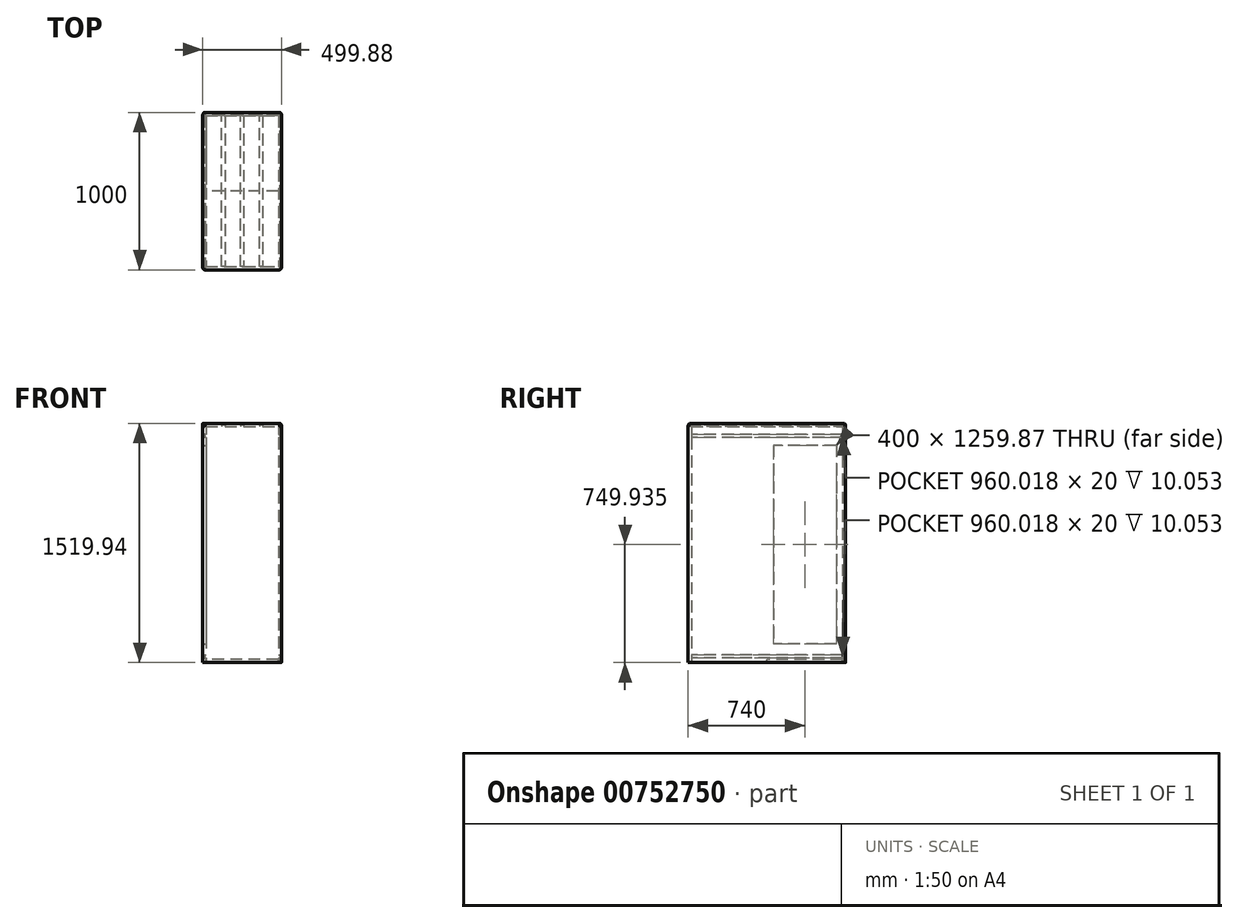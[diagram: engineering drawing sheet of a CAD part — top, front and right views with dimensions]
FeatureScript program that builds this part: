
annotation { "Feature Type Name" : "Feature", "Feature Type Description" : "" }
export const myFeature = defineFeature(function(context is Context, id is Id, definition is map)
    precondition{}
    {
        {
            var Q0;
            Q0=qCreatedBy(makeId("Top.planeOp"),FACE);
            var sketch = newSketch(context, id + "F0", { "sketchPlane" : qUnion([Q0])});
            skLineSegment(sketch, "E0.bottom", {"start": v(-249.94, -500) * mm, "end": v(249.94, -500) * mm});
            skLineSegment(sketch, "E0.top", {"start": v(-249.94, 500) * mm, "end": v(249.94, 500) * mm});
            skLineSegment(sketch, "E0.left", {"start": v(-249.94, -500) * mm, "end": v(-249.94, 500) * mm});
            skLineSegment(sketch, "E0.right", {"start": v(249.94, -500) * mm, "end": v(249.94, 500) * mm});
            skPoint(sketch, "E0.middle", {"position": v(0, 0) * mm});
            skLineSegment(sketch, "E1.0", {"start": v(-229.95, -480) * mm, "end": v(-229.95, 480) * mm});
            skLineSegment(sketch, "E1.1", {"start": v(-229.95, -480) * mm, "end": v(229.95, -480) * mm});
            skLineSegment(sketch, "E1.2", {"start": v(229.95, -480) * mm, "end": v(229.95, 480) * mm});
            skLineSegment(sketch, "E1.3", {"start": v(-229.95, 480) * mm, "end": v(229.95, 480) * mm});
            skLineSegment(sketch, "E2.top", {"start": v(-229.95, 0) * mm, "end": v(229.95, 0) * mm});
            skLineSegment(sketch, "E2.left", {"start": v(-229.95, -480) * mm, "end": v(-229.95, 0) * mm});
            skLineSegment(sketch, "E2.right", {"start": v(229.95, -480) * mm, "end": v(229.95, 0) * mm});
            skSolve(sketch);
        }
        {
            var Q0;
            Q0=makeQuery(id+"F0.imprint","IMPRINT",FACE,{"disambiguationData":[TD([[makeQuery(id+"F0.imprint","IMPRINT",EDGE,{"derivedFrom":sQuery(id+"F0.wireOp",EDGE,"E0.bottom")}),1.0]])]});
            extrude(context, id + "F1", {"entities" : qUnion([Q0]), "depth" : 5.9 * 254 * mm, "offsetDistance" : 25.4 * mm});
        }
        {
            var Q0;
            Q0=makeQuery(id+"F1.opExtrude","SWEPT_FACE",FACE,{"disambiguationData":[OSD([sQuery(id+"F0.wireOp",EDGE,"E0.right")])]});
            var sketch = newSketch(context, id + "F2", { "sketchPlane" : qUnion([Q0])});
            skLineSegment(sketch, "E3.bottom", {"start": v(-500, 1499.87) * mm, "end": v(500, 1499.87) * mm});
            skLineSegment(sketch, "E3.top", {"start": v(-500, 1519.94) * mm, "end": v(500, 1519.94) * mm});
            skLineSegment(sketch, "E3.left", {"start": v(-500, 1499.87) * mm, "end": v(-500, 1519.94) * mm});
            skLineSegment(sketch, "E3.right", {"start": v(500, 1499.87) * mm, "end": v(500, 1519.94) * mm});
            skSolve(sketch);
        }
        {
            var Q0;
            Q0=makeQuery(id+"F2.imprint","IMPRINT",FACE,{"disambiguationData":[TD([[makeQuery(id+"F2.imprint","IMPRINT",EDGE,{"derivedFrom":sQuery(id+"F2.wireOp",EDGE,"E3.bottom")}),1.0]])]});
            var Q1;
            Q1=makeQuery(id+"F1.opExtrude","SWEPT_FACE",FACE,{"disambiguationData":[OSD([sQuery(id+"F0.wireOp",EDGE,"E0.left")])]});
            extrude(context, id + "F3", {"entities" : qUnion([Q0]), "depth" : 0 * mm, "offsetDistance" : 25.4 * mm, "hasSecondDirection" : true, "secondDirectionBound" : SecondDirectionBoundingType.UP_TO_SURFACE, "secondDirectionOppositeDirection" : true, "secondDirectionDepth" : 25.4 * mm, "secondDirectionBoundEntityFace" : qUnion([Q1])});
        }
        {
            var Q0;
            Q0=qCreatedBy(makeId("Front.planeOp"),FACE);
            var sketch = newSketch(context, id + "F4", { "sketchPlane" : qUnion([Q0])});
            skLineSegment(sketch, "E4", {"start": v(0, 0) * mm, "end": v(0, 20) * mm});
            skLineSegment(sketch, "E5.bottom", {"start": v(-230, 1459.87) * mm, "end": v(230, 1459.87) * mm});
            skLineSegment(sketch, "E5.top", {"start": v(-230, 20) * mm, "end": v(230, 20) * mm});
            skLineSegment(sketch, "E5.left", {"start": v(-230, 1459.87) * mm, "end": v(-230, 20) * mm});
            skLineSegment(sketch, "E5.right", {"start": v(230, 1459.87) * mm, "end": v(230, 20) * mm});
            skPoint(sketch, "E6", {"position": v(0, 20) * mm});
            skLineSegment(sketch, "E7.bottom", {"start": v(-220, 1449.87) * mm, "end": v(-240, 1449.87) * mm});
            skLineSegment(sketch, "E7.top", {"start": v(-220, 1429.87) * mm, "end": v(-240, 1429.87) * mm});
            skLineSegment(sketch, "E7.left", {"start": v(-220, 1449.87) * mm, "end": v(-220, 1429.87) * mm});
            skLineSegment(sketch, "E7.right", {"start": v(-240, 1449.87) * mm, "end": v(-240, 1429.87) * mm});
            skPoint(sketch, "E7.middle", {"position": v(-230, 1439.87) * mm});
            skLineSegment(sketch, "E8", {"start": v(-230, 1439.87) * mm, "end": v(230, 1439.87) * mm});
            skLineSegment(sketch, "E9.bottom", {"start": v(220, 1449.87) * mm, "end": v(240, 1449.87) * mm});
            skLineSegment(sketch, "E9.top", {"start": v(220, 1429.87) * mm, "end": v(240, 1429.87) * mm});
            skLineSegment(sketch, "E9.left", {"start": v(220, 1449.87) * mm, "end": v(220, 1429.87) * mm});
            skLineSegment(sketch, "E9.right", {"start": v(240, 1449.87) * mm, "end": v(240, 1429.87) * mm});
            skPoint(sketch, "E9.middle", {"position": v(230, 1439.87) * mm});
            skLineSegment(sketch, "E10", {"start": v(-230, 1459.87) * mm, "end": v(-230, 1499.87) * mm});
            skLineSegment(sketch, "E11", {"start": v(-230, 1499.87) * mm, "end": v(230, 1499.87) * mm});
            skLineSegment(sketch, "E12", {"start": v(230, 1499.87) * mm, "end": v(230, 1459.87) * mm});
            skPoint(sketch, "E13", {"position": v(230, 1499.87) * mm});
            skPoint(sketch, "E14", {"position": v(-120, 1499.87) * mm});
            skPoint(sketch, "E15", {"position": v(0, 1499.87) * mm});
            skPoint(sketch, "E16", {"position": v(120, 1499.87) * mm});
            skLineSegment(sketch, "E17.bottom", {"start": v(-110, 1509.87) * mm, "end": v(-130, 1509.87) * mm});
            skLineSegment(sketch, "E17.top", {"start": v(-110, 1489.87) * mm, "end": v(-130, 1489.87) * mm});
            skLineSegment(sketch, "E17.left", {"start": v(-110, 1509.87) * mm, "end": v(-110, 1489.87) * mm});
            skLineSegment(sketch, "E17.right", {"start": v(-130, 1509.87) * mm, "end": v(-130, 1489.87) * mm});
            skLineSegment(sketch, "E18.bottom", {"start": v(130, 1509.87) * mm, "end": v(110, 1509.87) * mm});
            skLineSegment(sketch, "E18.top", {"start": v(130, 1489.87) * mm, "end": v(110, 1489.87) * mm});
            skLineSegment(sketch, "E18.left", {"start": v(130, 1509.87) * mm, "end": v(130, 1489.87) * mm});
            skLineSegment(sketch, "E18.right", {"start": v(110, 1509.87) * mm, "end": v(110, 1489.87) * mm});
            skLineSegment(sketch, "E19.bottom", {"start": v(10, 1509.87) * mm, "end": v(-10, 1509.87) * mm});
            skLineSegment(sketch, "E19.top", {"start": v(10, 1489.87) * mm, "end": v(-10, 1489.87) * mm});
            skLineSegment(sketch, "E19.left", {"start": v(10, 1509.87) * mm, "end": v(10, 1489.87) * mm});
            skLineSegment(sketch, "E19.right", {"start": v(-10, 1509.87) * mm, "end": v(-10, 1489.87) * mm});
            skLineSegment(sketch, "E20.bottom", {"start": v(220, 50) * mm, "end": v(240, 50) * mm});
            skLineSegment(sketch, "E20.top", {"start": v(220, 30) * mm, "end": v(240, 30) * mm});
            skLineSegment(sketch, "E20.left", {"start": v(220, 50) * mm, "end": v(220, 30) * mm});
            skLineSegment(sketch, "E20.right", {"start": v(240, 50) * mm, "end": v(240, 30) * mm});
            skPoint(sketch, "E20.middle", {"position": v(230, 40) * mm});
            skLineSegment(sketch, "E21.bottom", {"start": v(-240, 50) * mm, "end": v(-220, 50) * mm});
            skLineSegment(sketch, "E21.top", {"start": v(-240, 30) * mm, "end": v(-220, 30) * mm});
            skLineSegment(sketch, "E21.left", {"start": v(-240, 50) * mm, "end": v(-240, 30) * mm});
            skLineSegment(sketch, "E21.right", {"start": v(-220, 50) * mm, "end": v(-220, 30) * mm});
            skPoint(sketch, "E21.middle", {"position": v(-230, 40) * mm});
            skLineSegment(sketch, "E22.bottom", {"start": v(243.78, 1499.87) * mm, "end": v(238.18, 1499.87) * mm});
            skLineSegment(sketch, "E22.top", {"start": v(245.64, 1509.87) * mm, "end": v(236.32, 1509.87) * mm});
            skLineSegment(sketch, "E22.left", {"start": v(243.78, 1499.87) * mm, "end": v(245.64, 1509.87) * mm});
            skLineSegment(sketch, "E22.right", {"start": v(238.18, 1499.87) * mm, "end": v(236.32, 1509.87) * mm});
            skLineSegment(sketch, "E23.MirrorCS", {"start": v(-243.78, 1499.87) * mm, "end": v(-238.18, 1499.87) * mm});
            skLineSegment(sketch, "E24.MirrorCS", {"start": v(-238.18, 1499.87) * mm, "end": v(-236.32, 1509.87) * mm});
            skLineSegment(sketch, "E25.MirrorCS", {"start": v(-243.78, 1499.87) * mm, "end": v(-245.64, 1509.87) * mm});
            skLineSegment(sketch, "E26.MirrorCS", {"start": v(-245.64, 1509.87) * mm, "end": v(-236.32, 1509.87) * mm});
            skSolve(sketch);
        }
        {
            var Q0;
            Q0=qCreatedBy(makeId("Right.planeOp"),FACE);
            var sketch = newSketch(context, id + "F5", { "sketchPlane" : qUnion([Q0])});
            skLineSegment(sketch, "E27.bottom", {"start": v(0, 1419.87) * mm, "end": v(480, 1419.87) * mm});
            skLineSegment(sketch, "E27.top", {"start": v(0, 80) * mm, "end": v(480, 80) * mm});
            skLineSegment(sketch, "E27.left", {"start": v(0, 1419.87) * mm, "end": v(0, 80) * mm});
            skLineSegment(sketch, "E27.right", {"start": v(480, 1419.87) * mm, "end": v(480, 80) * mm});
            skLineSegment(sketch, "E28.bottom", {"start": v(20, 100) * mm, "end": v(460, 100) * mm});
            skLineSegment(sketch, "E28.top", {"start": v(20, 1399.87) * mm, "end": v(460, 1399.87) * mm});
            skLineSegment(sketch, "E28.left", {"start": v(20, 100) * mm, "end": v(20, 1399.87) * mm});
            skLineSegment(sketch, "E28.right", {"start": v(460, 100) * mm, "end": v(460, 1399.87) * mm});
            skLineSegment(sketch, "E29.0", {"start": v(440, 120) * mm, "end": v(440, 1379.87) * mm});
            skLineSegment(sketch, "E29.1", {"start": v(40, 120) * mm, "end": v(440, 120) * mm});
            skLineSegment(sketch, "E29.2", {"start": v(40, 120) * mm, "end": v(40, 1379.87) * mm});
            skLineSegment(sketch, "E29.3", {"start": v(40, 1379.87) * mm, "end": v(440, 1379.87) * mm});
            skSolve(sketch);
        }
        {
            var Q0;
            Q0=qCreatedBy(makeId("Front.planeOp"),FACE);
            var sketch = newSketch(context, id + "F6", { "sketchPlane" : qUnion([Q0])});
            skLineSegment(sketch, "E30.bottom", {"start": v(230, 0) * mm, "end": v(-230, 0) * mm});
            skLineSegment(sketch, "E30.top", {"start": v(230, 20) * mm, "end": v(-230, 20) * mm});
            skLineSegment(sketch, "E30.left", {"start": v(230, 0) * mm, "end": v(230, 20) * mm});
            skLineSegment(sketch, "E30.right", {"start": v(-230, 0) * mm, "end": v(-230, 20) * mm});
            skSolve(sketch);
        }
        {
            var Q0;
            Q0=makeQuery(id+"F6.imprint","IMPRINT",FACE,{"disambiguationData":[TD([[makeQuery(id+"F6.imprint","IMPRINT",EDGE,{"derivedFrom":sQuery(id+"F6.wireOp",EDGE,"E30.bottom")}),-1.0]])]});
            var Q1;
            Q1=makeQuery(id+"F1.opExtrude","SWEPT_FACE",FACE,{"disambiguationData":[OSD([sQuery(id+"F0.wireOp",EDGE,"E1.1")])]});
            var Q2;
            Q2=makeQuery(id+"F1.opExtrude","SWEPT_FACE",FACE,{"disambiguationData":[OSD([sQuery(id+"F0.wireOp",EDGE,"E1.3")])]});
            extrude(context, id + "F7", {"entities" : qUnion([Q0]), "depth" : 0 * mm, "endBoundEntityFace" : qUnion([Q1]), "offsetDistance" : 25.4 * mm, "hasSecondDirection" : true, "secondDirectionBound" : SecondDirectionBoundingType.UP_TO_SURFACE, "secondDirectionOppositeDirection" : true, "secondDirectionDepth" : 25.4 * mm, "secondDirectionBoundEntityFace" : qUnion([Q2])});
        }
        {
            var Q0;
            Q0=makeQuery(id+"F5.imprint","IMPRINT",FACE,{"disambiguationData":[TD([[makeQuery(id+"F5.imprint","IMPRINT",EDGE,{"derivedFrom":sQuery(id+"F5.wireOp",EDGE,"E29.0")}),1.0]])]});
            var Q1;
            Q1=makeQuery(id+"F1.opExtrude","SWEPT_FACE",FACE,{"disambiguationData":[OSD([sQuery(id+"F0.wireOp",EDGE,"E0.left")])]});
            extrude(context, id + "F8", {"entities" : qUnion([Q0]), "operationType" : NewBodyOperationType.REMOVE, "endBound" : BoundingType.UP_TO_SURFACE, "oppositeDirection" : true, "depth" : 0 * mm, "endBoundEntityFace" : qUnion([Q1]), "offsetDistance" : 25.4 * mm});
        }
        {
            var Q0;
            {var subQ5=sQuery(id+"F4.wireOp",EDGE,"E17.bottom");Q0=makeQuery(id+"F4.imprint","IMPRINT",FACE,{"disambiguationData":[TD([[makeQuery(id+"F4.imprint","IMPRINT",EDGE,{"derivedFrom":subQ5}),1.0]])]});}
            var Q1;
            {var subQ5=sQuery(id+"F4.wireOp",EDGE,"E17.top");Q1=makeQuery(id+"F4.imprint","IMPRINT",FACE,{"disambiguationData":[TD([[makeQuery(id+"F4.imprint","IMPRINT",EDGE,{"derivedFrom":subQ5}),-1.0]])]});}
            var Q2;
            {var subQ5=sQuery(id+"F4.wireOp",EDGE,"E19.bottom");Q2=makeQuery(id+"F4.imprint","IMPRINT",FACE,{"disambiguationData":[TD([[makeQuery(id+"F4.imprint","IMPRINT",EDGE,{"derivedFrom":subQ5}),1.0]])]});}
            var Q3;
            {var subQ5=sQuery(id+"F4.wireOp",EDGE,"E19.top");Q3=makeQuery(id+"F4.imprint","IMPRINT",FACE,{"disambiguationData":[TD([[makeQuery(id+"F4.imprint","IMPRINT",EDGE,{"derivedFrom":subQ5}),-1.0]])]});}
            var Q4;
            {var subQ5=sQuery(id+"F4.wireOp",EDGE,"E18.top");Q4=makeQuery(id+"F4.imprint","IMPRINT",FACE,{"disambiguationData":[TD([[makeQuery(id+"F4.imprint","IMPRINT",EDGE,{"derivedFrom":subQ5}),-1.0]])]});}
            var Q5;
            {var subQ5=sQuery(id+"F4.wireOp",EDGE,"E18.bottom");Q5=makeQuery(id+"F4.imprint","IMPRINT",FACE,{"disambiguationData":[TD([[makeQuery(id+"F4.imprint","IMPRINT",EDGE,{"derivedFrom":subQ5}),1.0]])]});}
            var Q6;
            {var subQ0=sQuery(id+"F4.wireOp",EDGE,"E9.right");Q6=makeQuery(id+"F4.imprint","IMPRINT",FACE,{"disambiguationData":[TD([[makeQuery(id+"F4.imprint","IMPRINT",EDGE,{"derivedFrom":subQ0}),-1.0]])]});}
            var Q7;
            {var subQ0=sQuery(id+"F4.wireOp",EDGE,"E8");var subQ1=sQuery(id+"F4.wireOp",EDGE,"E5.right");var subQ2=makeQuery(id+"F4.imprint","INTERSECT",VERTEX,{"derivedFrom":[subQ1,subQ0]});Q7=makeQuery(id+"F4.imprint","IMPRINT",FACE,{"disambiguationData":[TD([[makeQuery(id+"F4.imprint","IMPRINT",EDGE,{"disambiguationData":[TD([[subQ2,1.0]])],"derivedFrom":subQ1}),-1.0]])]});}
            var Q8;
            {var subQ0=sQuery(id+"F4.wireOp",EDGE,"E8");var subQ1=sQuery(id+"F4.wireOp",EDGE,"E5.right");var subQ2=makeQuery(id+"F4.imprint","INTERSECT",VERTEX,{"derivedFrom":[subQ1,subQ0]});Q8=makeQuery(id+"F4.imprint","IMPRINT",FACE,{"disambiguationData":[TD([[makeQuery(id+"F4.imprint","IMPRINT",EDGE,{"disambiguationData":[TD([[subQ2,-1.0]])],"derivedFrom":subQ1}),-1.0]])]});}
            var Q9;
            {var subQ0=sQuery(id+"F4.wireOp",EDGE,"E8");var subQ1=sQuery(id+"F4.wireOp",EDGE,"E5.left");var subQ2=makeQuery(id+"F4.imprint","INTERSECT",VERTEX,{"derivedFrom":[subQ1,subQ0]});Q9=makeQuery(id+"F4.imprint","IMPRINT",FACE,{"disambiguationData":[TD([[makeQuery(id+"F4.imprint","IMPRINT",EDGE,{"disambiguationData":[TD([[subQ2,-1.0]])],"derivedFrom":subQ1}),1.0]])]});}
            var Q10;
            {var subQ0=sQuery(id+"F4.wireOp",EDGE,"E8");var subQ1=sQuery(id+"F4.wireOp",EDGE,"E5.left");var subQ2=makeQuery(id+"F4.imprint","INTERSECT",VERTEX,{"derivedFrom":[subQ1,subQ0]});Q10=makeQuery(id+"F4.imprint","IMPRINT",FACE,{"disambiguationData":[TD([[makeQuery(id+"F4.imprint","IMPRINT",EDGE,{"disambiguationData":[TD([[subQ2,1.0]])],"derivedFrom":subQ1}),1.0]])]});}
            var Q11;
            {var subQ0=sQuery(id+"F4.wireOp",EDGE,"E7.right");Q11=makeQuery(id+"F4.imprint","IMPRINT",FACE,{"disambiguationData":[TD([[makeQuery(id+"F4.imprint","IMPRINT",EDGE,{"derivedFrom":subQ0}),1.0]])]});}
            var Q12;
            {var subQ5=sQuery(id+"F4.wireOp",EDGE,"E21.right");Q12=makeQuery(id+"F4.imprint","IMPRINT",FACE,{"disambiguationData":[TD([[makeQuery(id+"F4.imprint","IMPRINT",EDGE,{"derivedFrom":subQ5}),-1.0]])]});}
            var Q13;
            {var subQ5=sQuery(id+"F4.wireOp",EDGE,"E21.left");Q13=makeQuery(id+"F4.imprint","IMPRINT",FACE,{"disambiguationData":[TD([[makeQuery(id+"F4.imprint","IMPRINT",EDGE,{"derivedFrom":subQ5}),1.0]])]});}
            var Q14;
            {var subQ5=sQuery(id+"F4.wireOp",EDGE,"E20.right");Q14=makeQuery(id+"F4.imprint","IMPRINT",FACE,{"disambiguationData":[TD([[makeQuery(id+"F4.imprint","IMPRINT",EDGE,{"derivedFrom":subQ5}),-1.0]])]});}
            var Q15;
            {var subQ5=sQuery(id+"F4.wireOp",EDGE,"E20.left");Q15=makeQuery(id+"F4.imprint","IMPRINT",FACE,{"disambiguationData":[TD([[makeQuery(id+"F4.imprint","IMPRINT",EDGE,{"derivedFrom":subQ5}),1.0]])]});}
            var Q16;
            Q16=makeQuery(id+"F1.opExtrude","SWEPT_FACE",FACE,{"disambiguationData":[OSD([sQuery(id+"F0.wireOp",EDGE,"E1.3")])]});
            var Q17;
            Q17=makeQuery(id+"F1.opExtrude","SWEPT_FACE",FACE,{"disambiguationData":[OSD([sQuery(id+"F0.wireOp",EDGE,"E1.1")])]});
            extrude(context, id + "F9", {"entities" : qUnion([Q0, Q1, Q2, Q3, Q4, Q5, Q6, Q7, Q8, Q9, Q10, Q11, Q12, Q13, Q14, Q15]), "operationType" : NewBodyOperationType.REMOVE, "endBound" : BoundingType.UP_TO_SURFACE, "oppositeDirection" : true, "depth" : 25.4 * mm, "endBoundEntityFace" : qUnion([Q16]), "offsetDistance" : 25.4 * mm, "hasSecondDirection" : true, "secondDirectionBound" : SecondDirectionBoundingType.UP_TO_SURFACE, "secondDirectionOppositeDirection" : false, "secondDirectionDepth" : 25.4 * mm, "secondDirectionBoundEntityFace" : qUnion([Q17])});
        }
        {
            var Q0;
            Q0=makeQuery(id+"F4.imprint","IMPRINT",FACE,{"disambiguationData":[TD([[makeQuery(id+"F4.imprint","IMPRINT",EDGE,{"derivedFrom":sQuery(id+"F4.wireOp",EDGE,"E22.bottom")}),-1.0]])]});
            var Q1;
            Q1=makeQuery(id+"F4.imprint","IMPRINT",FACE,{"disambiguationData":[TD([[makeQuery(id+"F4.imprint","IMPRINT",EDGE,{"derivedFrom":sQuery(id+"F4.wireOp",EDGE,"E23.MirrorCS")}),1.0]])]});
            var Q2;
            Q2=makeQuery(id+"F1.opExtrude","SWEPT_FACE",FACE,{"disambiguationData":[OSD([sQuery(id+"F0.wireOp",EDGE,"E0.bottom")])]});
            var Q3;
            Q3=makeQuery(id+"F1.opExtrude","SWEPT_FACE",FACE,{"disambiguationData":[OSD([sQuery(id+"F0.wireOp",EDGE,"E0.top")])]});
            extrude(context, id + "F10", {"entities" : qUnion([Q0, Q1]), "operationType" : NewBodyOperationType.ADD, "endBound" : BoundingType.UP_TO_SURFACE, "depth" : 25.4 * mm, "endBoundEntityFace" : qUnion([Q2]), "offsetDistance" : 25.4 * mm, "hasSecondDirection" : true, "secondDirectionBound" : SecondDirectionBoundingType.UP_TO_SURFACE, "secondDirectionOppositeDirection" : true, "secondDirectionDepth" : 25.4 * mm, "secondDirectionBoundEntityFace" : qUnion([Q3])});
        }
        {
            var Q0;
            Q0=makeQuery(id+"F4.imprint","IMPRINT",FACE,{"disambiguationData":[TD([[makeQuery(id+"F4.imprint","IMPRINT",EDGE,{"derivedFrom":sQuery(id+"F4.wireOp",EDGE,"E22.bottom")}),-1.0]])]});
            var Q1;
            Q1=makeQuery(id+"F4.imprint","IMPRINT",FACE,{"disambiguationData":[TD([[makeQuery(id+"F4.imprint","IMPRINT",EDGE,{"derivedFrom":sQuery(id+"F4.wireOp",EDGE,"E23.MirrorCS")}),1.0]])]});
            extrude(context, id + "F11", {"entities" : qUnion([Q0, Q1]), "operationType" : NewBodyOperationType.REMOVE, "endBound" : BoundingType.UP_TO_NEXT, "oppositeDirection" : true, "depth" : 25.4 * mm, "offsetDistance" : 25.4 * mm, "hasSecondDirection" : true, "secondDirectionBound" : SecondDirectionBoundingType.UP_TO_NEXT, "secondDirectionOppositeDirection" : false, "secondDirectionDepth" : 25.4 * mm});
        }
        {
            var Q0;
            Q0=makeQuery(id+"F1.opExtrude","SWEPT_EDGE",EDGE,{"disambiguationData":[OSD([sQuery(id+"F0.wireOp",EDGE,"E0.top"),sQuery(id+"F0.wireOp",EDGE,"E0.right")])]});
            var Q1;
            Q1=makeQuery(id+"F1.opExtrude","SWEPT_EDGE",EDGE,{"disambiguationData":[OSD([sQuery(id+"F0.wireOp",EDGE,"E0.top"),sQuery(id+"F0.wireOp",EDGE,"E0.left")])]});
            var Q2;
            Q2=makeQuery(id+"F3.opExtrude","SWEPT_EDGE",EDGE,{"disambiguationData":[OSD([sQuery(id+"F2.wireOp",EDGE,"E3.top"),sQuery(id+"F2.wireOp",EDGE,"E3.right")])]});
            var Q3;
            Q3=makeQuery(id+"F3.opExtrude","TWEAK_EDGE",EDGE,{"derivedFrom":[makeQuery(id+"F1.opExtrude","SWEPT_FACE",FACE,{"disambiguationData":[OSD([sQuery(id+"F0.wireOp",EDGE,"E0.left")])]}),makeQuery(id+"F2.imprint","IMPRINT",EDGE,{"derivedFrom":sQuery(id+"F2.wireOp",EDGE,"E3.top")})]});
            var Q4;
            Q4=makeQuery(id+"F3.opExtrude","CAP_EDGE",EDGE,{"disambiguationData":[OSD([sQuery(id+"F2.wireOp",EDGE,"E3.top")])],"isStart":false});
            var Q5;
            Q5=makeQuery(id+"F1.opExtrude","SWEPT_EDGE",EDGE,{"disambiguationData":[OSD([sQuery(id+"F0.wireOp",EDGE,"E0.bottom"),sQuery(id+"F0.wireOp",EDGE,"E0.right")])]});
            var Q6;
            Q6=makeQuery(id+"F3.opExtrude","SWEPT_EDGE",EDGE,{"disambiguationData":[OSD([sQuery(id+"F2.wireOp",EDGE,"E3.top"),sQuery(id+"F2.wireOp",EDGE,"E3.left")])]});
            var Q7;
            Q7=makeQuery(id+"F1.opExtrude","SWEPT_EDGE",EDGE,{"disambiguationData":[OSD([sQuery(id+"F0.wireOp",EDGE,"E0.bottom"),sQuery(id+"F0.wireOp",EDGE,"E0.left")])]});
            var Q8;
            Q8=makeQuery(id+"F3.opExtrude","CAP_EDGE",EDGE,{"disambiguationData":[OSD([sQuery(id+"F2.wireOp",EDGE,"E3.right")])],"isStart":false});
            var Q9;
            Q9=makeQuery(id+"F3.opExtrude","TWEAK_EDGE",EDGE,{"derivedFrom":[makeQuery(id+"F1.opExtrude","SWEPT_FACE",FACE,{"disambiguationData":[OSD([sQuery(id+"F0.wireOp",EDGE,"E0.left")])]}),makeQuery(id+"F2.imprint","IMPRINT",EDGE,{"derivedFrom":sQuery(id+"F2.wireOp",EDGE,"E3.right")})]});
            var Q10;
            Q10=makeQuery(id+"F3.opExtrude","TWEAK_EDGE",EDGE,{"derivedFrom":[makeQuery(id+"F1.opExtrude","SWEPT_FACE",FACE,{"disambiguationData":[OSD([sQuery(id+"F0.wireOp",EDGE,"E0.left")])]}),makeQuery(id+"F2.imprint","IMPRINT",EDGE,{"derivedFrom":sQuery(id+"F2.wireOp",EDGE,"E3.left")})]});
            var Q11;
            Q11=makeQuery(id+"F3.opExtrude","CAP_EDGE",EDGE,{"disambiguationData":[OSD([sQuery(id+"F2.wireOp",EDGE,"E3.left")])],"isStart":false});
            fillet(context, id + "F12", {"entities" : qUnion([Q0, Q1, Q2, Q3, Q4, Q5, Q6, Q7, Q8, Q9, Q10, Q11]), "radius" : 15.24 * mm, "tangentPropagation" : true, "allowEdgeOverflow" : false});
        }
    });
